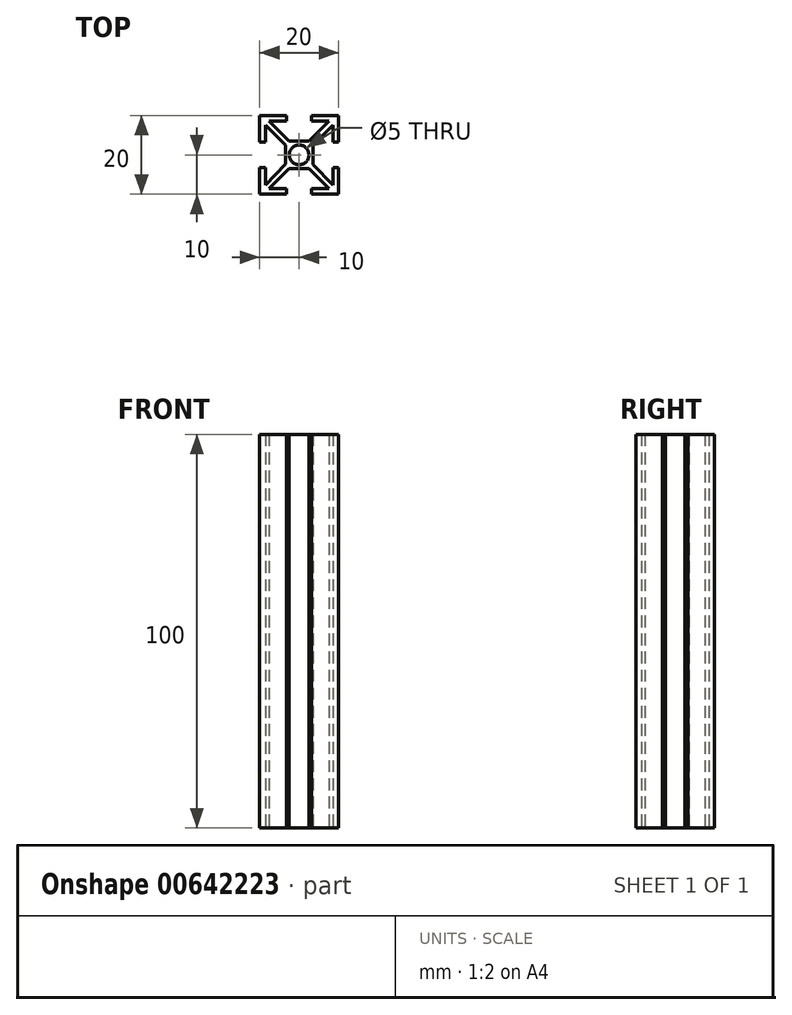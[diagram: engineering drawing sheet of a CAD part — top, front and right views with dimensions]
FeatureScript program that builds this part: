
annotation { "Feature Type Name" : "Feature", "Feature Type Description" : "" }
export const myFeature = defineFeature(function(context is Context, id is Id, definition is map)
    precondition{}
    {
        {
            var Q0;
            Q0=qCreatedBy(makeId("Top.planeOp"),FACE);
            var sketch = newSketch(context, id + "F0", { "sketchPlane" : qUnion([Q0])});
            skCircle(sketch, "E0", {"center": v(10, 10) * mm, "radius": 2.5 * mm});
            skLineSegment(sketch, "E1", {"start": v(0, 0) * mm, "end": v(10, 10) * mm, "construction": true});
            skLineSegment(sketch, "E2", {"start": v(1.4, 2.39) * mm, "end": v(1.4, 6.8) * mm});
            skLineSegment(sketch, "E3", {"start": v(1.4, 6.8) * mm, "end": v(0, 6.8) * mm});
            skLineSegment(sketch, "E4", {"start": v(0, 6.8) * mm, "end": v(0, 0) * mm});
            skLineSegment(sketch, "E5", {"start": v(7.49, 6.5) * mm, "end": v(2.39, 1.4) * mm});
            skLineSegment(sketch, "E6", {"start": v(2.39, 1.4) * mm, "end": v(6.8, 1.4) * mm});
            skLineSegment(sketch, "E7", {"start": v(6.8, 1.4) * mm, "end": v(6.8, 0) * mm});
            skLineSegment(sketch, "E8", {"start": v(6.8, 0) * mm, "end": v(0, 0) * mm});
            skLineSegment(sketch, "E9", {"start": v(10, 10) * mm, "end": v(20, 20) * mm, "construction": true});
            skLineSegment(sketch, "E10", {"start": v(10, 10) * mm, "end": v(0, 20) * mm, "construction": true});
            skLineSegment(sketch, "E11", {"start": v(10, 10) * mm, "end": v(20, 0) * mm, "construction": true});
            skLineSegment(sketch, "E12", {"start": v(1.4, 17.61) * mm, "end": v(6.5, 12.51) * mm});
            skLineSegment(sketch, "E13", {"start": v(1.4, 17.61) * mm, "end": v(1.4, 13.2) * mm});
            skLineSegment(sketch, "E14", {"start": v(1.4, 13.2) * mm, "end": v(0, 13.2) * mm});
            skLineSegment(sketch, "E15", {"start": v(0, 13.2) * mm, "end": v(0, 20) * mm});
            skLineSegment(sketch, "E16", {"start": v(7.49, 13.5) * mm, "end": v(2.39, 18.6) * mm});
            skLineSegment(sketch, "E17", {"start": v(2.39, 18.6) * mm, "end": v(6.8, 18.6) * mm});
            skLineSegment(sketch, "E18", {"start": v(6.8, 18.6) * mm, "end": v(6.8, 20) * mm});
            skLineSegment(sketch, "E19", {"start": v(6.8, 20) * mm, "end": v(0, 20) * mm});
            skLineSegment(sketch, "E20", {"start": v(12.51, 13.5) * mm, "end": v(17.61, 18.6) * mm});
            skLineSegment(sketch, "E21", {"start": v(17.61, 18.6) * mm, "end": v(13.2, 18.6) * mm});
            skLineSegment(sketch, "E22", {"start": v(13.2, 18.6) * mm, "end": v(13.2, 20) * mm});
            skLineSegment(sketch, "E23", {"start": v(13.2, 20) * mm, "end": v(20, 20) * mm});
            skLineSegment(sketch, "E24", {"start": v(13.5, 12.51) * mm, "end": v(18.6, 17.61) * mm});
            skLineSegment(sketch, "E25", {"start": v(18.6, 17.61) * mm, "end": v(18.6, 13.2) * mm});
            skLineSegment(sketch, "E26", {"start": v(18.6, 13.2) * mm, "end": v(20, 13.2) * mm});
            skLineSegment(sketch, "E27", {"start": v(20, 13.2) * mm, "end": v(20, 20) * mm});
            skLineSegment(sketch, "E28", {"start": v(18.6, 2.39) * mm, "end": v(18.6, 6.8) * mm});
            skLineSegment(sketch, "E29", {"start": v(18.6, 6.8) * mm, "end": v(20, 6.8) * mm});
            skLineSegment(sketch, "E30", {"start": v(20, 6.8) * mm, "end": v(20, 0) * mm});
            skLineSegment(sketch, "E31", {"start": v(12.51, 6.5) * mm, "end": v(17.61, 1.4) * mm});
            skLineSegment(sketch, "E32", {"start": v(17.61, 1.4) * mm, "end": v(13.2, 1.4) * mm});
            skLineSegment(sketch, "E33", {"start": v(13.2, 1.4) * mm, "end": v(13.2, 0) * mm});
            skLineSegment(sketch, "E34", {"start": v(13.2, 0) * mm, "end": v(20, 0) * mm});
            skLineSegment(sketch, "E35", {"start": v(12.51, 6.5) * mm, "end": v(7.49, 6.5) * mm});
            skLineSegment(sketch, "E36", {"start": v(7.49, 13.5) * mm, "end": v(12.51, 13.5) * mm});
            skLineSegment(sketch, "E37", {"start": v(10, 10) * mm, "end": v(10, 0) * mm, "construction": true});
            skLineSegment(sketch, "E38", {"start": v(10, 10) * mm, "end": v(18.77, 10) * mm, "construction": true});
            skLineSegment(sketch, "E39", {"start": v(10, 10) * mm, "end": v(10, 20.74) * mm, "construction": true});
            skLineSegment(sketch, "E40", {"start": v(10, 10) * mm, "end": v(0, 10) * mm, "construction": true});
            skLineSegment(sketch, "E41.bottom", {"start": v(0, 0) * mm, "end": v(20, 0) * mm, "construction": true});
            skLineSegment(sketch, "E41.top", {"start": v(0, 20) * mm, "end": v(20, 20) * mm, "construction": true});
            skLineSegment(sketch, "E41.left", {"start": v(0, 0) * mm, "end": v(0, 20) * mm, "construction": true});
            skLineSegment(sketch, "E41.right", {"start": v(20, 0) * mm, "end": v(20, 20) * mm, "construction": true});
            skLineSegment(sketch, "E42", {"start": v(18.6, 2.39) * mm, "end": v(13.5, 7.49) * mm});
            skLineSegment(sketch, "E43", {"start": v(13.5, 7.49) * mm, "end": v(13.5, 12.51) * mm});
            skLineSegment(sketch, "E44", {"start": v(1.4, 2.39) * mm, "end": v(6.5, 7.62) * mm});
            skLineSegment(sketch, "E45", {"start": v(6.5, 7.62) * mm, "end": v(6.5, 12.51) * mm});
            skSolve(sketch);
        }
        {
            var Q0;
            Q0=makeQuery(id+"F0.imprint","IMPRINT",FACE,{"disambiguationData":[TD([[makeQuery(id+"F0.imprint","IMPRINT",EDGE,{"derivedFrom":sQuery(id+"F0.wireOp",EDGE,"E0")}),-1.0]])]});
            extrude(context, id + "F1", {"entities" : qUnion([Q0]), "depth" : 100 * mm, "offsetDistance" : 25 * mm});
        }
    });
